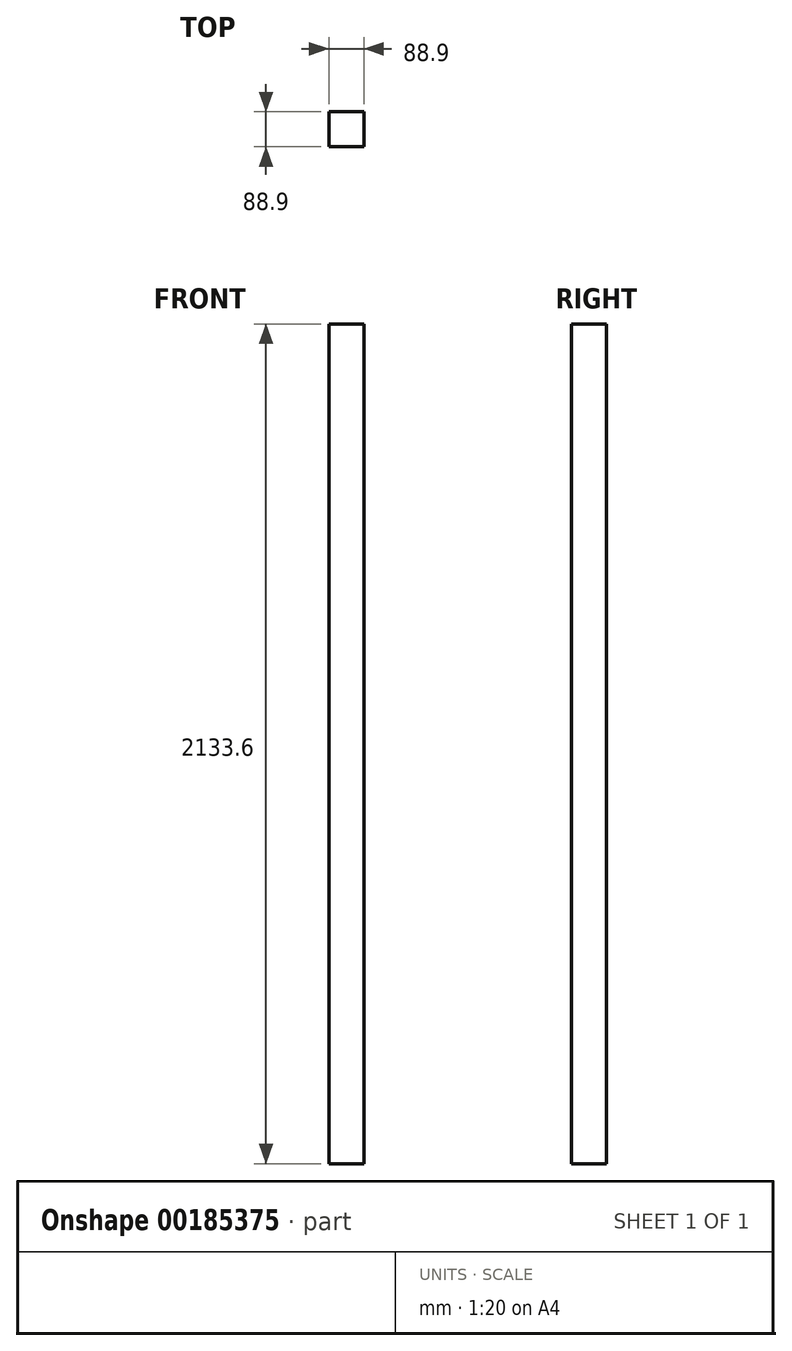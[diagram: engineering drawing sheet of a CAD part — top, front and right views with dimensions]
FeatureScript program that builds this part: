
annotation { "Feature Type Name" : "Feature", "Feature Type Description" : "" }
export const myFeature = defineFeature(function(context is Context, id is Id, definition is map)
    precondition{}
    {
        {
            var Q0;
            Q0=qCreatedBy(makeId("Top.planeOp"),FACE);
            var sketch = newSketch(context, id + "F0", { "sketchPlane" : qUnion([Q0])});
            skLineSegment(sketch, "E0.bottom", {"start": v(0, 0) * mm, "end": v(88.9, 0) * mm});
            skLineSegment(sketch, "E0.top", {"start": v(0, 88.9) * mm, "end": v(88.9, 88.9) * mm});
            skLineSegment(sketch, "E0.left", {"start": v(0, 0) * mm, "end": v(0, 88.9) * mm});
            skLineSegment(sketch, "E0.right", {"start": v(88.9, 0) * mm, "end": v(88.9, 88.9) * mm});
            skSolve(sketch);
        }
        {
            var Q0;
            Q0=makeQuery(id+"F0.imprint","IMPRINT",FACE,{"disambiguationData":[TD([[makeQuery(id+"F0.imprint","IMPRINT",EDGE,{"derivedFrom":sQuery(id+"F0.wireOp",EDGE,"E0.bottom")}),1.0]])]});
            extrude(context, id + "F1", {"entities" : qUnion([Q0]), "depth" : 2133.6 * mm});
        }
    });
